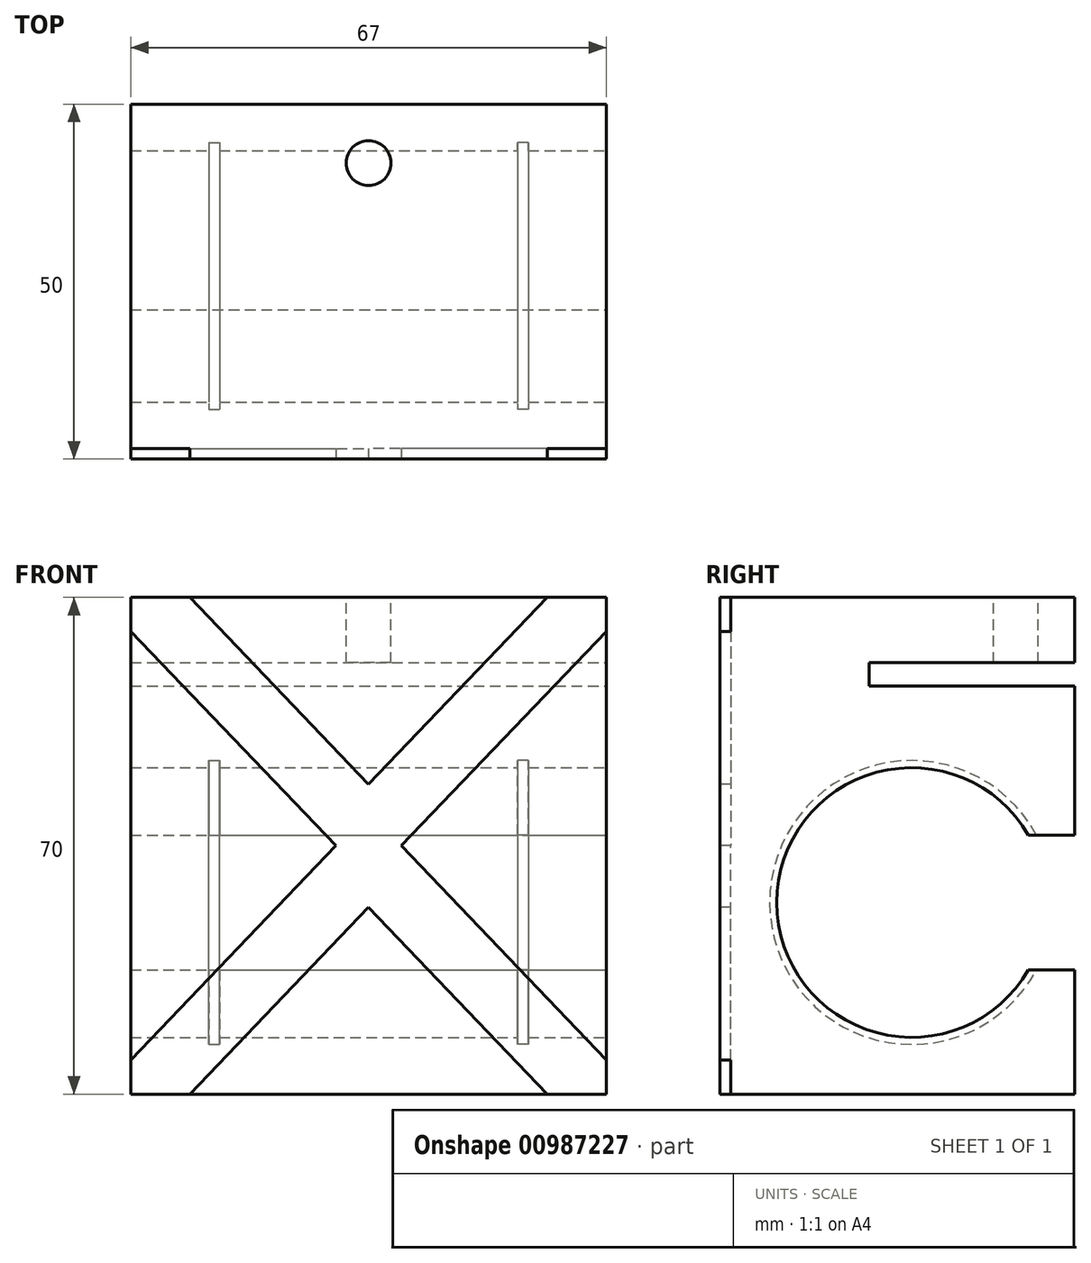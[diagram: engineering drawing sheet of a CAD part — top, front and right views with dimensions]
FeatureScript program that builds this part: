
annotation { "Feature Type Name" : "Feature", "Feature Type Description" : "" }
export const myFeature = defineFeature(function(context is Context, id is Id, definition is map)
    precondition{}
    {
        {
            var Q0;
            Q0=qCreatedBy(makeId("Top.planeOp"),FACE);
            var sketch = newSketch(context, id + "F0", { "sketchPlane" : qUnion([Q0])});
            skLineSegment(sketch, "E0.bottom", {"start": v(0, 0) * mm, "end": v(67, 0) * mm});
            skLineSegment(sketch, "E0.top", {"start": v(0, 50) * mm, "end": v(67, 50) * mm});
            skLineSegment(sketch, "E0.left", {"start": v(0, 0) * mm, "end": v(0, 50) * mm});
            skLineSegment(sketch, "E0.right", {"start": v(67, 0) * mm, "end": v(67, 50) * mm});
            skSolve(sketch);
        }
        {
            var Q0;
            Q0 = qSketchRegion(id + "F0", true);
            extrude(context, id + "F1", {"entities" : qUnion([Q0]), "depth" : 70 * mm, "offsetDistance" : 25.4 * mm});
        }
        {
            var Q0;
            Q0=makeQuery(id+"F1.opExtrude","SWEPT_FACE",FACE,{"disambiguationData":[OSD([sQuery(id+"F0.wireOp",EDGE,"E0.bottom")])]});
            var sketch = newSketch(context, id + "F2", { "sketchPlane" : qUnion([Q0])});
            skLineSegment(sketch, "E1", {"start": v(0, 70) * mm, "end": v(8.31, 70) * mm});
            skLineSegment(sketch, "E2", {"start": v(0, 70) * mm, "end": v(0, 65.2) * mm});
            skLineSegment(sketch, "E3", {"start": v(58.69, 70) * mm, "end": v(67, 70) * mm});
            skLineSegment(sketch, "E4", {"start": v(67, 70) * mm, "end": v(67, 65.2) * mm});
            skLineSegment(sketch, "E5", {"start": v(0, 4.8) * mm, "end": v(0, 0) * mm});
            skLineSegment(sketch, "E6", {"start": v(0, 0) * mm, "end": v(8.31, 0) * mm});
            skLineSegment(sketch, "E7", {"start": v(58.69, 0) * mm, "end": v(67, 0) * mm});
            skLineSegment(sketch, "E8", {"start": v(67, 0) * mm, "end": v(67, 4.8) * mm});
            skLineSegment(sketch, "E9", {"start": v(0, 70) * mm, "end": v(67, 0) * mm, "construction": true});
            skLineSegment(sketch, "E10", {"start": v(67, 70) * mm, "end": v(0, 0) * mm, "construction": true});
            skLineSegment(sketch, "E11", {"start": v(8.31, 70) * mm, "end": v(33.5, 43.69) * mm});
            skLineSegment(sketch, "E12", {"start": v(0, 65.2) * mm, "end": v(28.9, 35) * mm});
            skLineSegment(sketch, "E13", {"start": v(58.69, 70) * mm, "end": v(33.5, 43.69) * mm});
            skLineSegment(sketch, "E14", {"start": v(67, 65.2) * mm, "end": v(38.1, 35) * mm});
            skLineSegment(sketch, "E15", {"start": v(0, 4.8) * mm, "end": v(28.9, 35) * mm});
            skLineSegment(sketch, "E16", {"start": v(8.31, 0) * mm, "end": v(33.5, 26.31) * mm});
            skLineSegment(sketch, "E17", {"start": v(58.69, 0) * mm, "end": v(33.5, 26.31) * mm});
            skLineSegment(sketch, "E18", {"start": v(67, 4.8) * mm, "end": v(38.1, 35) * mm});
            skSolve(sketch);
        }
        {
            var Q0;
            Q0 = qSketchRegion(id + "F2", true);
            extrude(context, id + "F3", {"entities" : qUnion([Q0]), "operationType" : NewBodyOperationType.REMOVE, "oppositeDirection" : true, "depth" : 1.5 * mm, "offsetDistance" : 25.4 * mm});
        }
        {
            var Q0;
            Q0=makeQuery(id+"F1.opExtrude","SWEPT_FACE",FACE,{"disambiguationData":[OSD([sQuery(id+"F0.wireOp",EDGE,"E0.right")])]});
            var sketch = newSketch(context, id + "F4", { "sketchPlane" : qUnion([Q0])});
            skArc(sketch, "E19", {"start": v(43.45, 36.5) * mm, "mid": v(8, 27) * mm, "end": v(43.45, 17.5) * mm});
            skLineSegment(sketch, "E20.bottom", {"start": v(50, 57.5) * mm, "end": v(21, 57.5) * mm});
            skLineSegment(sketch, "E20.top", {"start": v(50, 60.8) * mm, "end": v(21, 60.8) * mm});
            skLineSegment(sketch, "E20.left", {"start": v(50, 60.8) * mm, "end": v(50, 57.5) * mm});
            skLineSegment(sketch, "E20.right", {"start": v(21, 60.8) * mm, "end": v(21, 57.5) * mm});
            skLineSegment(sketch, "E21.bottom", {"start": v(50, 36.5) * mm, "end": v(43.45, 36.5) * mm});
            skLineSegment(sketch, "E21.top", {"start": v(50, 17.5) * mm, "end": v(43.45, 17.5) * mm});
            skLineSegment(sketch, "E21.left", {"start": v(50, 36.5) * mm, "end": v(50, 17.5) * mm});
            skSolve(sketch);
        }
        {
            var Q0;
            Q0 = qSketchRegion(id + "F4", true);
            extrude(context, id + "F5", {"entities" : qUnion([Q0]), "operationType" : NewBodyOperationType.REMOVE, "endBound" : BoundingType.THROUGH_ALL, "oppositeDirection" : true, "depth" : 25.4 * mm, "offsetDistance" : 25.4 * mm});
        }
        {
            var Q0;
            Q0=makeQuery(id+"F1.opExtrude","CAP_FACE",FACE,{"disambiguationData":[OSD([sQuery(id+"F0.wireOp",EDGE,"E0.bottom"),sQuery(id+"F0.wireOp",EDGE,"E0.top"),sQuery(id+"F0.wireOp",EDGE,"E0.left"),sQuery(id+"F0.wireOp",EDGE,"E0.right")])],"isStart":false});
            var sketch = newSketch(context, id + "F6", { "sketchPlane" : qUnion([Q0])});
            skCircle(sketch, "E22", {"center": v(33.5, 41.7) * mm, "radius": 3.15 * mm});
            skSolve(sketch);
        }
        {
            var Q0;
            Q0 = qSketchRegion(id + "F6", true);
            var Q1;
            Q1=makeQuery(id+"F5.boolean.opBoolean","COPY",FACE,{"derivedFrom":makeQuery(id+"F5.opExtrude","SWEPT_FACE",FACE,{"disambiguationData":[OSD([sQuery(id+"F4.wireOp",EDGE,"E20.top")])]})});
            extrude(context, id + "F7", {"entities" : qUnion([Q0]), "operationType" : NewBodyOperationType.REMOVE, "endBound" : BoundingType.UP_TO_SURFACE, "oppositeDirection" : true, "depth" : 25.4 * mm, "endBoundEntityFace" : qUnion([Q1]), "offsetDistance" : 25.4 * mm});
        }
        {
            var Q0;
            Q0=makeQuery(id+"F1.opExtrude","SWEPT_FACE",FACE,{"disambiguationData":[OSD([sQuery(id+"F0.wireOp",EDGE,"E0.right")])]});
            cPlane(context, id + "F8", {"entities" : qUnion([Q0]), "cplaneType" : CPlaneType.OFFSET, "offset" : 12.5 * mm, "oppositeDirection" : true, "width" : 152.4 * mm, "height" : 152.4 * mm});
        }
        {
            var Q0;
            Q0=qCreatedBy(id+"F8.planeOp",FACE);
            var sketch = newSketch(context, id + "F9", { "sketchPlane" : qUnion([Q0])});
            skCircle(sketch, "E23", {"center": v(27, 27) * mm, "radius": 20 * mm});
            skSolve(sketch);
        }
        {
            var Q0;
            Q0 = qSketchRegion(id + "F9", true);
            extrude(context, id + "F10", {"entities" : qUnion([Q0]), "operationType" : NewBodyOperationType.REMOVE, "depth" : 1.5 * mm, "offsetDistance" : 25.4 * mm});
        }
        {
            var Q0;
            Q0=makeQuery(id+"F1.opExtrude","SWEPT_FACE",FACE,{"disambiguationData":[OSD([sQuery(id+"F0.wireOp",EDGE,"E0.left")])]});
            cPlane(context, id + "F11", {"entities" : qUnion([Q0]), "cplaneType" : CPlaneType.OFFSET, "offset" : 12.5 * mm, "oppositeDirection" : true, "width" : 152.4 * mm, "height" : 152.4 * mm});
        }
        {
            var Q0;
            Q0=qCreatedBy(id+"F11.planeOp",FACE);
            var sketch = newSketch(context, id + "F12", { "sketchPlane" : qUnion([Q0])});
            skCircle(sketch, "E24", {"center": v(-27, 27) * mm, "radius": 20 * mm});
            skSolve(sketch);
        }
        {
            var Q0;
            Q0 = qSketchRegion(id + "F12", true);
            extrude(context, id + "F13", {"entities" : qUnion([Q0]), "operationType" : NewBodyOperationType.REMOVE, "depth" : 1.5 * mm, "offsetDistance" : 25.4 * mm});
        }
    });
